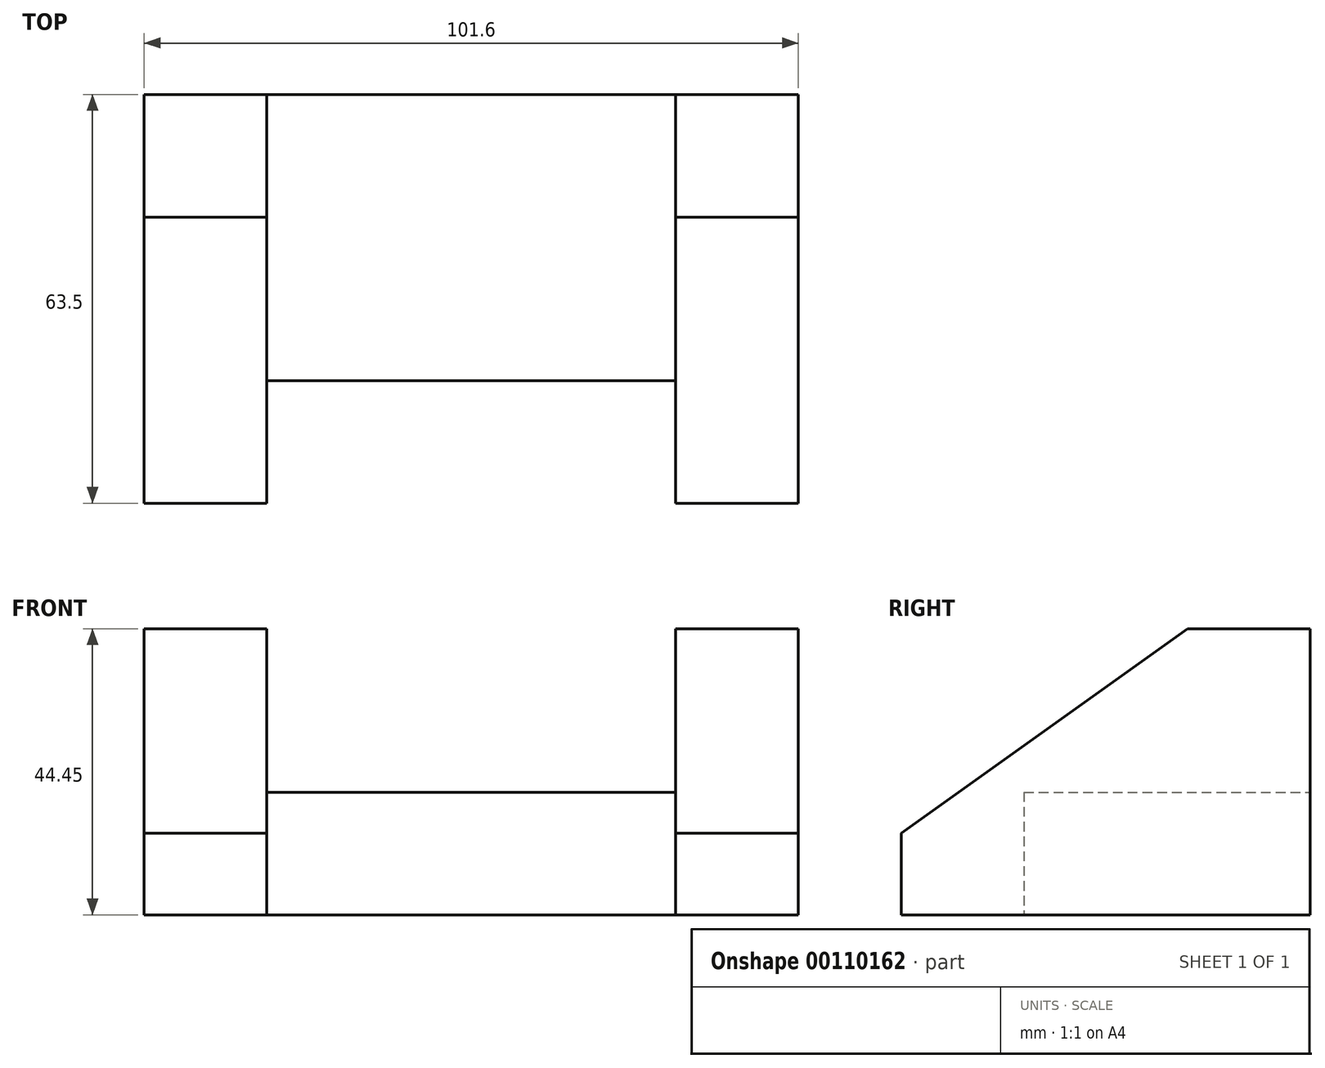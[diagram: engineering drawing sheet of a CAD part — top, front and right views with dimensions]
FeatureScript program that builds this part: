
annotation { "Feature Type Name" : "Feature", "Feature Type Description" : "" }
export const myFeature = defineFeature(function(context is Context, id is Id, definition is map)
    precondition{}
    {
        {
            var Q0;
            Q0=qCreatedBy(makeId("Front.planeOp"),FACE);
            var sketch = newSketch(context, id + "F0", { "sketchPlane" : qUnion([Q0])});
            skLineSegment(sketch, "E0.bottom", {"start": v(-24.34, 25.4) * mm, "end": v(-43.4, 25.4) * mm});
            skLineSegment(sketch, "E0.top", {"start": v(-24.34, -19.05) * mm, "end": v(-43.4, -19.05) * mm});
            skLineSegment(sketch, "E0.left", {"start": v(-24.34, 25.4) * mm, "end": v(-24.34, -19.05) * mm});
            skLineSegment(sketch, "E0.right", {"start": v(-43.4, 25.4) * mm, "end": v(-43.4, -19.05) * mm});
            skLineSegment(sketch, "E1.bottom", {"start": v(39.16, 25.4) * mm, "end": v(58.2, 25.4) * mm});
            skLineSegment(sketch, "E1.top", {"start": v(39.16, -19.05) * mm, "end": v(58.2, -19.05) * mm});
            skLineSegment(sketch, "E1.left", {"start": v(39.16, 25.4) * mm, "end": v(39.16, -19.05) * mm});
            skLineSegment(sketch, "E1.right", {"start": v(58.2, 25.4) * mm, "end": v(58.2, -19.05) * mm});
            skLineSegment(sketch, "E2.bottom", {"start": v(-24.34, 0) * mm, "end": v(39.16, 0) * mm});
            skLineSegment(sketch, "E2.top", {"start": v(-24.34, -19.05) * mm, "end": v(39.16, -19.05) * mm});
            skLineSegment(sketch, "E2.left", {"start": v(-24.34, 0) * mm, "end": v(-24.34, -19.05) * mm});
            skLineSegment(sketch, "E2.right", {"start": v(39.16, 0) * mm, "end": v(39.16, -19.05) * mm});
            skLineSegment(sketch, "E3", {"start": v(-43.4, -6.35) * mm, "end": v(-24.34, -6.35) * mm});
            skLineSegment(sketch, "E4", {"start": v(39.16, -6.35) * mm, "end": v(58.2, -6.35) * mm});
            skLineSegment(sketch, "E5", {"start": v(-43.4, 30.52) * mm, "end": v(-24.34, 30.52) * mm});
            skLineSegment(sketch, "E6", {"start": v(39.16, 30.52) * mm, "end": v(58.2, 30.52) * mm});
            skSolve(sketch);
        }
        {
            var Q0;
            Q0 = qSketchRegion(id + "F0", true);
            extrude(context, id + "F1", {"entities" : qUnion([Q0]), "depth" : 63.5 * mm});
        }
        {
            var Q0;
            Q0=makeQuery(id+"F1.opExtrude","SWEPT_FACE",FACE,{"disambiguationData":[OSD([sQuery(id+"F0.wireOp",EDGE,"E1.right")])]});
            var sketch = newSketch(context, id + "F2", { "sketchPlane" : qUnion([Q0])});
            skLineSegment(sketch, "E7", {"start": v(-63.5, -6.35) * mm, "end": v(-63.5, -19.05) * mm});
            skLineSegment(sketch, "E8", {"start": v(-63.5, -19.05) * mm, "end": v(0, -19.05) * mm});
            skLineSegment(sketch, "E9", {"start": v(0, -19.05) * mm, "end": v(0, 25.4) * mm});
            skLineSegment(sketch, "E10", {"start": v(0, 25.4) * mm, "end": v(-19.05, 25.4) * mm});
            skLineSegment(sketch, "E11", {"start": v(-63.5, -6.35) * mm, "end": v(-19.05, 25.4) * mm});
            skSolve(sketch);
        }
        {
            var Q0;
            Q0=makeQuery(id+"F1.opExtrude","CAP_FACE",FACE,{"disambiguationData":[OSD([sQuery(id+"F0.wireOp",EDGE,"E0.bottom"),sQuery(id+"F0.wireOp",EDGE,"E0.top"),sQuery(id+"F0.wireOp",EDGE,"E0.left"),sQuery(id+"F0.wireOp",EDGE,"E0.right"),sQuery(id+"F0.wireOp",EDGE,"E1.bottom"),sQuery(id+"F0.wireOp",EDGE,"E1.top"),sQuery(id+"F0.wireOp",EDGE,"E1.left"),sQuery(id+"F0.wireOp",EDGE,"E1.right"),sQuery(id+"F0.wireOp",EDGE,"E2.bottom"),sQuery(id+"F0.wireOp",EDGE,"E2.top")])],"isStart":false});
            var sketch = newSketch(context, id + "F3", { "sketchPlane" : qUnion([Q0])});
            skLineSegment(sketch, "E12", {"start": v(-24.34, 0) * mm, "end": v(-24.34, -19.05) * mm});
            skLineSegment(sketch, "E13", {"start": v(39.16, 0) * mm, "end": v(39.16, -19.05) * mm});
            skSolve(sketch);
        }
        {
            var Q0;
            {var subQ0=sQuery(id+"F3.wireOp",EDGE,"E12");Q0=makeQuery(id+"F3.imprint","IMPRINT",FACE,{"disambiguationData":[TD([[makeQuery(id+"F3.imprint","IMPRINT",EDGE,{"derivedFrom":subQ0}),1.0]])]});}
            extrude(context, id + "F4", {"entities" : qUnion([Q0]), "operationType" : NewBodyOperationType.REMOVE, "oppositeDirection" : true, "depth" : 19.05 * mm});
        }
        {
            var Q0;
            {var subQ0=sQuery(id+"F2.wireOp",EDGE,"E11");Q0=makeQuery(id+"F2.imprint","IMPRINT",FACE,{"disambiguationData":[TD([[makeQuery(id+"F2.imprint","IMPRINT",EDGE,{"derivedFrom":subQ0}),1.0]])]});}
            extrude(context, id + "F5", {"entities" : qUnion([Q0]), "operationType" : NewBodyOperationType.REMOVE, "oppositeDirection" : true, "depth" : 40 * mm});
        }
        {
            var Q0;
            Q0=makeQuery(id+"F1.opExtrude","SWEPT_FACE",FACE,{"disambiguationData":[OSD([sQuery(id+"F0.wireOp",EDGE,"E0.right")])]});
            var sketch = newSketch(context, id + "F6", { "sketchPlane" : qUnion([Q0])});
            skLineSegment(sketch, "E14", {"start": v(63.5, -19.05) * mm, "end": v(63.5, -6.35) * mm});
            skLineSegment(sketch, "E15", {"start": v(63.5, -19.05) * mm, "end": v(0, -19.05) * mm});
            skLineSegment(sketch, "E16", {"start": v(0, -19.05) * mm, "end": v(0, 25.4) * mm});
            skLineSegment(sketch, "E17", {"start": v(0, 25.4) * mm, "end": v(19.05, 25.4) * mm});
            skLineSegment(sketch, "E18", {"start": v(19.05, 25.4) * mm, "end": v(63.5, -6.35) * mm});
            skSolve(sketch);
        }
        {
            var Q0;
            {var subQ0=sQuery(id+"F6.wireOp",EDGE,"E18");Q0=makeQuery(id+"F6.imprint","IMPRINT",FACE,{"disambiguationData":[TD([[makeQuery(id+"F6.imprint","IMPRINT",EDGE,{"derivedFrom":subQ0}),1.0]])]});}
            extrude(context, id + "F7", {"entities" : qUnion([Q0]), "operationType" : NewBodyOperationType.REMOVE, "oppositeDirection" : true, "depth" : 47.63 * mm});
        }
    });
